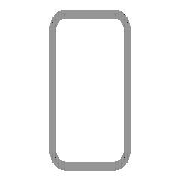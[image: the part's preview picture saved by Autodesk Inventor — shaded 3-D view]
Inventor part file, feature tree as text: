
AUTODESK INVENTOR PART (.ipt)
format: ipt  version: 2025 (Build 290162010, 162A)  size: 129,024 bytes
history: native  units: mm (DEFAULTED — no unit token found)
features: other x3, sketch x1, plane x1
ambient origin geometry x8: Origin, YZ Plane, XZ Plane, XY Plane, X Axis, Y Axis, Z Axis, Center Point
bodies: Solid1 (feature_tree), Body (feature_tree)
feature tree (5):
  other  "Driven Length"
  other  "Start plane"
  other  "End plane"
  sketch  "Sketch3"  dims[d3=1000.0mm d4=0.0mm d7=6.0mm d9=40.0mm d11=60.0mm d12=3.0mm d13=-0.0mm d14=1000.0mm d15=20.0mm d16=30.0mm d17=90.0deg d18=1000.0mm]
  plane  "Work Plane3"
